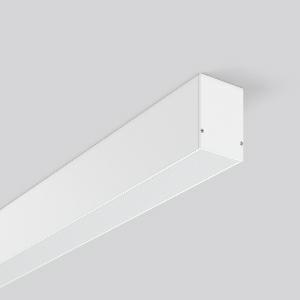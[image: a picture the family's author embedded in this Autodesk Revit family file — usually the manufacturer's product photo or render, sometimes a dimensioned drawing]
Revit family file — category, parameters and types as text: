
# Revit family: less_is_more_50_312309_002_1_76_1a97
name_source: partatom
category: Lighting Fixtures
units: mm (PartAtom-declared; Revit-internal decimal feet)

## family parameters
Cut with Voids When Loaded = No
Host = Face
Light Source = No
Part Type = Normal
Room Calculation Point = No
Round Connector Dimension = Use Diameter
Shared = No

## types (1)
- LESS IS MORE 50 (1 x LED Modul 840, 5650 lm, 4000)
    Apparent Load = 47 VA
    CIE Flux Codes = 48 79 95 100 100
    Color Rendering = 80
    Color Temperature = 4000
    Default Elevation = 1800 mm
    Description = Series: LESS IS MORE 50
Linear ceiling and wall luminaire for aesthetically sophisticated lighting. Housing: extruded aluminium profile, powder-coated. End cap aluminium powder-coated. Diffuser made of non-yellowing plastic (PMMA), opal. Suitable for Ceiling mounting. LED unit with integrated converter interchangeable and removable. Suitable for through-wiring. With sensors or as a safety luminaire on request. 
Colour: traffic white, matt (RAL 9016)
Length: 1967 mm
Width: 57 mm
Height: 75 mm
Lamp: LED
Socket: without socket
Colour temperature: 4000K
Colour rendering index (CRI): 80
System power: 47 W
Rated luminous flux: 5650 lm
Luminous efficiency: 120 lm/W
Control gear: Converter, dimmable, DALI
Protection class: I
Type of protection: IP 20
    Height = 75 mm
    Lamp = 1 x LED Modul 840
    Lamp Light Flux = 5650 lm
    Lamp count = 1
    Length = 1967 mm
    Lifetime = 50000 h
    Luminous efficacy = 120 lm/W
    Manufacturer = RZB
    ModVariant = No
    Model = 312309.002.1.76
    Mounting Place = Ceiling
    Mounting Type = Surface mounted
    Number of Poles = 1
    OnlyDefault = Yes
    Power Factor = 1
    Product Name = LESS IS MORE 50
    Product group = Surface mounted ceiling LED linear luminaires
    ProductGroupID = 312
    Protection Class = Protection class I
    Protection Degree = IP 20
    RLX_Detail_Level = 1
    RLX_Emergency_Light_Flux = 0 lm
    RLX_Emergency_Type = 0
    RLX_Emergency_Type_DB = No
    RlxData = <blob elided: 21413 chars, md5=77709a23>
    Socket = socket
    Standby Power = 0 W
    System Light Flux = 5650 lm
    System Power = 47 W
    Type Comments = Product without accessories
    Type Image = 312306.002.jpg
    URL = http://relux.com
    VarID = ---
    Voltage = 230 V
    Voltage Range = 220-240 V
    Weight = 0.00 kg
    Width = 57 mm

## geometry (parser evidence)
native form markers: Blend x4, Sweep x11
no freeform markers — native parametric forms only
